# Revit family: O60701001_Sanitario Solare
name_source: partatom
category: Plumbing Fixtures
units: mm (PartAtom-declared; Revit-internal decimal feet)

## family parameters
Always vertical = Yes
Cut with Voids When Loaded = No
Host = Wall
OmniClass Number = 23.31.19.17
Part Type = Normal
Room Calculation Point = No
Round Connector Dimension = Use Diameter
Shared = No

## types (1)
- Type 1
    Alto = 708 mm  [stored 2.32283 ft]
    Altura de sello = 5.5 cm
    Ancho = 415 mm  [stored 1.36155 ft]
    Capacidad de descarga = 800 gr
    Consumo de agua = 4.8 Lpf. 1.25 gpf.
    Creado por = BIMBAU
    Default Elevation = 0 mm  [stored 0 ft]
    Description = El diseño contínuo y limpio del sanitario Solare Single, representa la fluidez de las formas orgánicas creando un producto que integra el bienestar y la funcionalidad.
    Espejo de agua = 24.5 cm x 16.3 cm (9.5 pulg x 6.5 pulg)
    Fecha de creación = 11/03/2021
    Garantía = Integral
    Longitud = 717 mm  [stored 2.35236 ft]
    Manufacturer = Corona
    Material = Corona_Porcelana_Sanitaria_Blanco
    Material 2 = Corona_Cromado
    Model = Sanitario Solare
    Peso Bruto aprox = 46.614 kg
    Peso Neto aprox = 44.184 kg
    Presión de agua = 20 a 80 PSI
    URL = https://corona.co

note: [stored X ft] marks values corroborated as IEEE doubles in the binary element streams (Revit-internal decimal feet)

## geometry (parser evidence)
native form markers: Sweep x7
no freeform markers — native parametric forms only
